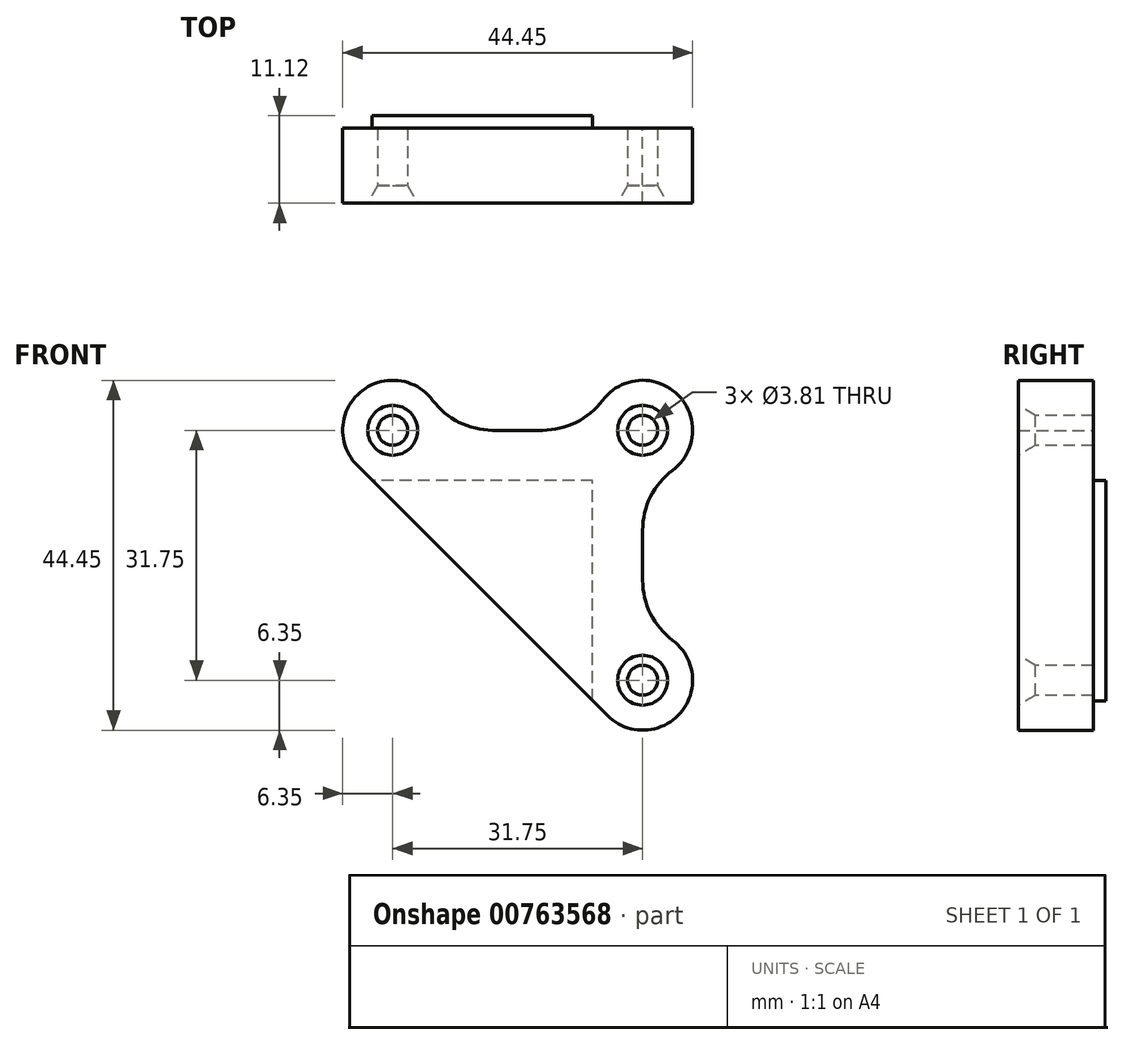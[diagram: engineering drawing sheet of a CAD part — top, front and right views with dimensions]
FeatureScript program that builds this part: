
annotation { "Feature Type Name" : "Feature", "Feature Type Description" : "" }
export const myFeature = defineFeature(function(context is Context, id is Id, definition is map)
    precondition{}
    {
        {
            var Q0;
            Q0=qCreatedBy(makeId("Front.planeOp"),FACE);
            var sketch = newSketch(context, id + "F0", { "sketchPlane" : qUnion([Q0])});
            skLineSegment(sketch, "E0", {"start": v(-12.7, 12.7) * mm, "end": v(-12.7, 0) * mm, "construction": true});
            skLineSegment(sketch, "E1", {"start": v(-12.7, 0) * mm, "end": v(0, 0) * mm, "construction": true});
            skLineSegment(sketch, "E2", {"start": v(0, 0) * mm, "end": v(0, -12.7) * mm, "construction": true});
            skLineSegment(sketch, "E3", {"start": v(0, -12.7) * mm, "end": v(12.7, -12.7) * mm, "construction": true});
            skLineSegment(sketch, "E4", {"start": v(12.7, -12.7) * mm, "end": v(12.7, 12.7) * mm, "construction": true});
            skLineSegment(sketch, "E5", {"start": v(12.7, 12.7) * mm, "end": v(-12.7, 12.7) * mm, "construction": true});
            skArc(sketch, "E6", {"start": v(-7.62, 22.86) * mm, "mid": v(-18.38, 21.89) * mm, "end": v(-12.7, 12.7) * mm});
            skArc(sketch, "E7", {"start": v(22.86, 13.97) * mm, "mid": v(23.54, 23.54) * mm, "end": v(13.97, 22.86) * mm});
            skArc(sketch, "E8", {"start": v(12.7, -12.7) * mm, "mid": v(21.89, -18.38) * mm, "end": v(22.86, -7.62) * mm});
            skLineSegment(sketch, "E9", {"start": v(0, 0) * mm, "end": v(19.05, 19.05) * mm, "construction": true});
            skLineSegment(sketch, "E10", {"start": v(19.05, -12.7) * mm, "end": v(19.05, 19.05) * mm, "construction": true});
            skLineSegment(sketch, "E11", {"start": v(-12.7, 19.05) * mm, "end": v(19.05, 19.05) * mm, "construction": true});
            skLineSegment(sketch, "E12", {"start": v(0, 19.05) * mm, "end": v(6.35, 19.05) * mm});
            skLineSegment(sketch, "E13", {"start": v(19.05, 6.35) * mm, "end": v(19.05, 0) * mm});
            skLineSegment(sketch, "E14", {"start": v(12.7, -12.7) * mm, "end": v(12.7, 12.7) * mm});
            skLineSegment(sketch, "E15", {"start": v(12.7, 12.7) * mm, "end": v(-12.7, 12.7) * mm});
            skPoint(sketch, "E16.visualSharp", {"position": v(-6.35, 19.05) * mm});
            skArc(sketch, "E16.filletArc", {"start": v(-7.62, 22.86) * mm, "mid": v(-4.26, 20.06) * mm, "end": v(0, 19.05) * mm});
            skPoint(sketch, "E17.visualSharp", {"position": v(12.7, 19.05) * mm});
            skArc(sketch, "E17.filletArc", {"start": v(6.35, 19.05) * mm, "mid": v(10.6, 20.06) * mm, "end": v(13.97, 22.86) * mm});
            skPoint(sketch, "E18.visualSharp", {"position": v(19.05, 12.7) * mm});
            skArc(sketch, "E18.filletArc", {"start": v(22.86, 13.97) * mm, "mid": v(20.06, 10.6) * mm, "end": v(19.05, 6.35) * mm});
            skPoint(sketch, "E19.visualSharp", {"position": v(19.05, -6.35) * mm});
            skArc(sketch, "E19.filletArc", {"start": v(19.05, 0) * mm, "mid": v(20.06, -4.26) * mm, "end": v(22.86, -7.62) * mm});
            skSolve(sketch);
        }
        {
            var Q0;
            Q0 = qSketchRegion(id + "F0", true);
            extrude(context, id + "F1", {"entities" : qUnion([Q0]), "depth" : 9.52 * mm, "offsetDistance" : 25.4 * mm});
        }
        {
            var Q0;
            Q0=makeQuery(id+"F1.opExtrude","CAP_FACE",FACE,{"disambiguationData":[OSD([sQuery(id+"F0.wireOp",EDGE,"E6"),sQuery(id+"F0.wireOp",EDGE,"E7"),sQuery(id+"F0.wireOp",EDGE,"E8"),sQuery(id+"F0.wireOp",EDGE,"E12"),sQuery(id+"F0.wireOp",EDGE,"E13"),sQuery(id+"F0.wireOp",EDGE,"E14"),sQuery(id+"F0.wireOp",EDGE,"E15"),sQuery(id+"F0.wireOp",EDGE,"E16.filletArc"),sQuery(id+"F0.wireOp",EDGE,"E17.filletArc"),sQuery(id+"F0.wireOp",EDGE,"E18.filletArc"),sQuery(id+"F0.wireOp",EDGE,"E19.filletArc")])],"isStart":false});
            var sketch = newSketch(context, id + "F2", { "sketchPlane" : qUnion([Q0])});
            skPoint(sketch, "E20", {"position": v(-12.7, 19.05) * mm});
            skPoint(sketch, "E21", {"position": v(19.05, 19.05) * mm});
            skPoint(sketch, "E22", {"position": v(19.05, -12.7) * mm});
            skSolve(sketch);
        }
        {
            var Q0;
            Q0=sQuery(id+"F2.wireOp",VERTEX,"E20");
            var Q1;
            Q1=sQuery(id+"F2.wireOp",VERTEX,"E21");
            var Q2;
            Q2=sQuery(id+"F2.wireOp",VERTEX,"E22");
            var Q3;
            Q3=makeQuery(id+"F1.opExtrude","SWEPT_BODY",BODY,{"disambiguationData":[OSD([sQuery(id+"F0.wireOp",EDGE,"E6"),sQuery(id+"F0.wireOp",EDGE,"E7"),sQuery(id+"F0.wireOp",EDGE,"E8"),sQuery(id+"F0.wireOp",EDGE,"E12"),sQuery(id+"F0.wireOp",EDGE,"E13"),sQuery(id+"F0.wireOp",EDGE,"E14"),sQuery(id+"F0.wireOp",EDGE,"E15"),sQuery(id+"F0.wireOp",EDGE,"E16.filletArc"),sQuery(id+"F0.wireOp",EDGE,"E17.filletArc"),sQuery(id+"F0.wireOp",EDGE,"E18.filletArc"),sQuery(id+"F0.wireOp",EDGE,"E19.filletArc")])]});
            hole(context, id + "F3", {"style" : HoleStyle.C_SINK, "endStyle" : HoleEndStyle.THROUGH, "holeDiameter" : 3.8 * mm, "cSinkDiameter" : 6.35 * mm, "cSinkAngle" : 60 * degree, "majorDiameter" : 6.35 * mm, "isTappedThrough" : true, "tappedDepth" : 12.7 * mm, "tapClearance" : 3, "startFromSketch" : true, "locations" : qUnion([Q0, Q1, Q2]), "scope" : qUnion([Q3])});
        }
        {
            var Q0;
            Q0=qCreatedBy(makeId("Front.planeOp"),FACE);
            var sketch = newSketch(context, id + "F4", { "sketchPlane" : qUnion([Q0])});
            skLineSegment(sketch, "E23.0", {"start": v(12.7, 12.7) * mm, "end": v(-12.7, 12.7) * mm});
            skArc(sketch, "E24.0", {"start": v(-17.2, 14.56) * mm, "mid": v(-15.13, 13.18) * mm, "end": v(-12.7, 12.7) * mm});
            skLineSegment(sketch, "E25.0", {"start": v(12.7, -12.7) * mm, "end": v(12.7, 12.7) * mm});
            skArc(sketch, "E26.0", {"start": v(12.7, -12.7) * mm, "mid": v(13.18, -15.13) * mm, "end": v(14.56, -17.2) * mm});
            skLineSegment(sketch, "E27", {"start": v(-17.2, 14.56) * mm, "end": v(14.56, -17.2) * mm});
            skPoint(sketch, "E28.orphan", {"position": v(-7.62, 22.86) * mm});
            skPoint(sketch, "E29.orphan", {"position": v(22.86, -7.62) * mm});
            skSolve(sketch);
        }
        {
            var Q0;
            Q0 = qSketchRegion(id + "F4", true);
            extrude(context, id + "F5", {"entities" : qUnion([Q0]), "operationType" : NewBodyOperationType.ADD, "depth" : 9.52 * mm, "offsetDistance" : 25.4 * mm, "hasSecondDirection" : true, "secondDirectionOppositeDirection" : true, "secondDirectionDepth" : 1.59 * mm});
        }
        {
            var Q0;
            Q0=makeQuery(id+"F1.opExtrude","CAP_FACE",FACE,{"disambiguationData":[OSD([sQuery(id+"F0.wireOp",EDGE,"E6"),sQuery(id+"F0.wireOp",EDGE,"E7"),sQuery(id+"F0.wireOp",EDGE,"E8"),sQuery(id+"F0.wireOp",EDGE,"E12"),sQuery(id+"F0.wireOp",EDGE,"E13"),sQuery(id+"F0.wireOp",EDGE,"E14"),sQuery(id+"F0.wireOp",EDGE,"E15"),sQuery(id+"F0.wireOp",EDGE,"E16.filletArc"),sQuery(id+"F0.wireOp",EDGE,"E17.filletArc"),sQuery(id+"F0.wireOp",EDGE,"E18.filletArc"),sQuery(id+"F0.wireOp",EDGE,"E19.filletArc")])],"isStart":true});
            var sketch = newSketch(context, id + "F6", { "sketchPlane" : qUnion([Q0])});
            skLineSegment(sketch, "E30.0", {"start": v(-12.7, -12.7) * mm, "end": v(-12.7, 12.7) * mm});
            skLineSegment(sketch, "E31.0", {"start": v(-12.7, 12.7) * mm, "end": v(12.7, 12.7) * mm});
            skLineSegment(sketch, "E32", {"start": v(-12.7, -12.7) * mm, "end": v(-12.7, -24.8) * mm});
            skLineSegment(sketch, "E33", {"start": v(-12.7, -24.8) * mm, "end": v(-31.78, -24.8) * mm});
            skLineSegment(sketch, "E34", {"start": v(-31.78, -24.8) * mm, "end": v(-31.78, 20.13) * mm});
            skLineSegment(sketch, "E35", {"start": v(-31.78, 20.13) * mm, "end": v(24.82, 21.18) * mm});
            skLineSegment(sketch, "E36", {"start": v(24.82, 21.18) * mm, "end": v(24.98, 12.7) * mm});
            skLineSegment(sketch, "E37", {"start": v(24.98, 12.7) * mm, "end": v(12.7, 12.7) * mm});
            skSolve(sketch);
        }
        {
            var Q0;
            Q0 = qSketchRegion(id + "F6", true);
            extrude(context, id + "F7", {"entities" : qUnion([Q0]), "operationType" : NewBodyOperationType.REMOVE, "depth" : 25.4 * mm, "offsetDistance" : 25.4 * mm});
        }
    });
